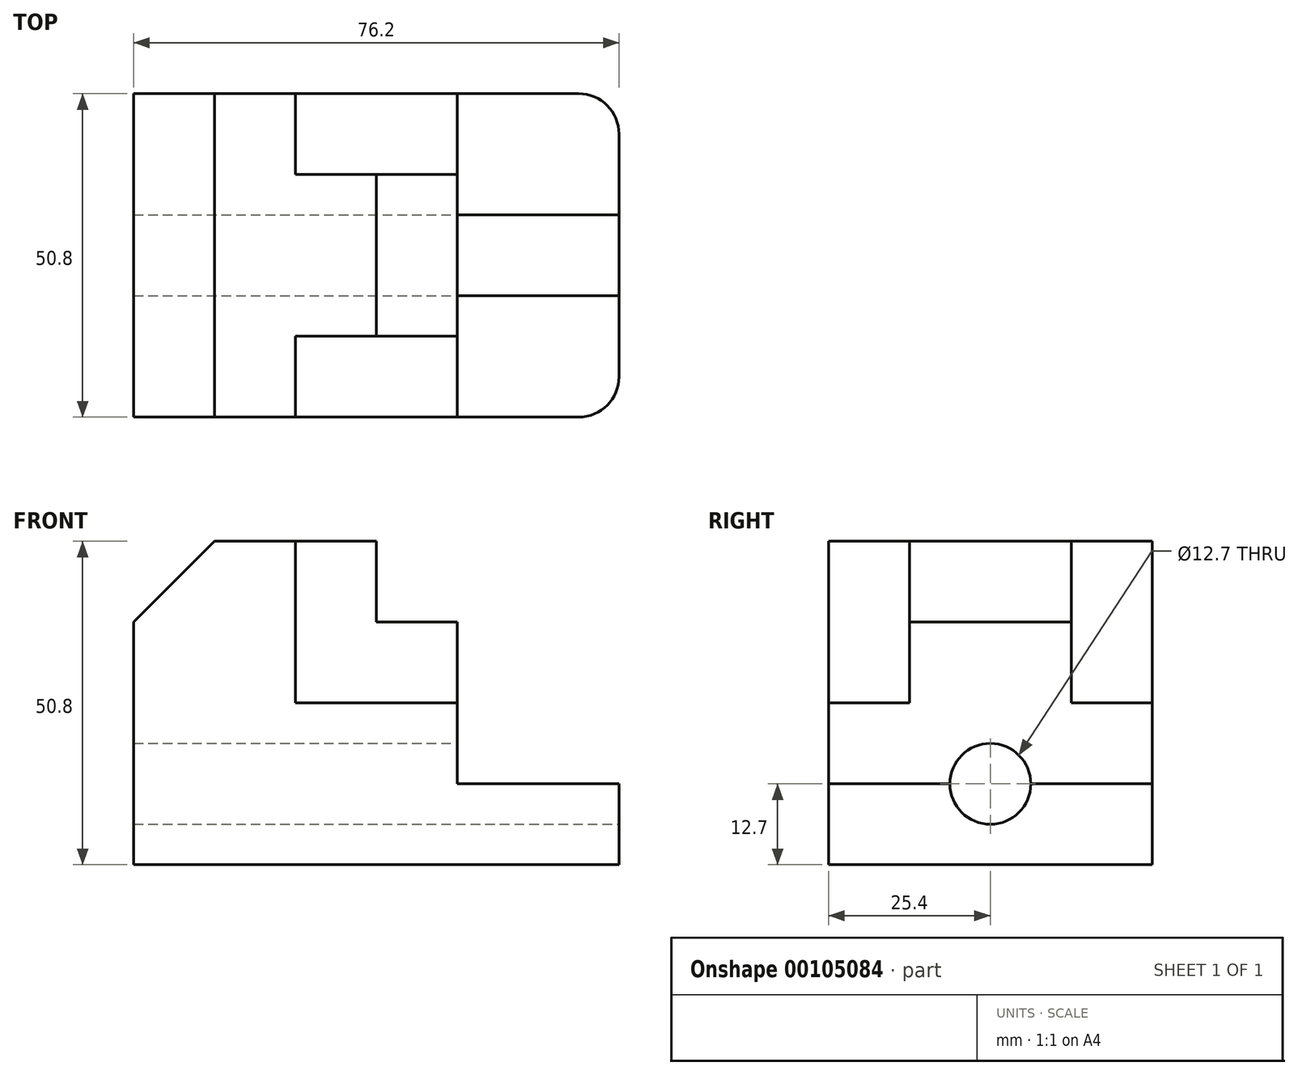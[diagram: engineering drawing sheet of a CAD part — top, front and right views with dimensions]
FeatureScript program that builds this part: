
annotation { "Feature Type Name" : "Feature", "Feature Type Description" : "" }
export const myFeature = defineFeature(function(context is Context, id is Id, definition is map)
    precondition{}
    {
        {
            var Q0;
            Q0=qCreatedBy(makeId("Front.planeOp"),FACE);
            var sketch = newSketch(context, id + "F0", { "sketchPlane" : qUnion([Q0])});
            skLineSegment(sketch, "E0.bottom", {"start": v(0, 0) * mm, "end": v(76.2, 0) * mm});
            skLineSegment(sketch, "E0.top", {"start": v(0, 50.8) * mm, "end": v(76.2, 50.8) * mm});
            skLineSegment(sketch, "E0.left", {"start": v(0, 0) * mm, "end": v(0, 50.8) * mm});
            skLineSegment(sketch, "E0.right", {"start": v(76.2, 0) * mm, "end": v(76.2, 50.8) * mm});
            skSolve(sketch);
        }
        {
            var Q0;
            Q0 = qSketchRegion(id + "F0", true);
            extrude(context, id + "F1", {"entities" : qUnion([Q0]), "depth" : 50.8 * mm});
        }
        {
            var Q0;
            Q0=makeQuery(id+"F1.opExtrude","CAP_FACE",FACE,{"disambiguationData":[OSD([sQuery(id+"F0.wireOp",EDGE,"E0.bottom"),sQuery(id+"F0.wireOp",EDGE,"E0.top"),sQuery(id+"F0.wireOp",EDGE,"E0.left"),sQuery(id+"F0.wireOp",EDGE,"E0.right")])],"isStart":false});
            var sketch = newSketch(context, id + "F2", { "sketchPlane" : qUnion([Q0])});
            skLineSegment(sketch, "E1", {"start": v(0, 50.8) * mm, "end": v(12.7, 50.8) * mm});
            skLineSegment(sketch, "E2", {"start": v(12.7, 50.8) * mm, "end": v(0, 38.1) * mm});
            skLineSegment(sketch, "E3", {"start": v(0, 38.1) * mm, "end": v(0, 50.8) * mm});
            skLineSegment(sketch, "E4", {"start": v(76.2, 50.8) * mm, "end": v(38.1, 50.8) * mm});
            skLineSegment(sketch, "E5", {"start": v(38.1, 50.8) * mm, "end": v(38.1, 38.1) * mm});
            skLineSegment(sketch, "E6", {"start": v(38.1, 38.1) * mm, "end": v(50.8, 38.1) * mm});
            skLineSegment(sketch, "E7", {"start": v(50.8, 38.1) * mm, "end": v(50.8, 12.7) * mm});
            skLineSegment(sketch, "E8", {"start": v(50.8, 12.7) * mm, "end": v(76.2, 12.7) * mm});
            skLineSegment(sketch, "E9", {"start": v(76.2, 12.7) * mm, "end": v(76.2, 50.8) * mm});
            skSolve(sketch);
        }
        {
            var Q0;
            Q0 = qSketchRegion(id + "F2", true);
            extrude(context, id + "F3", {"entities" : qUnion([Q0]), "operationType" : NewBodyOperationType.REMOVE, "endBound" : BoundingType.THROUGH_ALL, "oppositeDirection" : true, "depth" : 25.4 * mm});
        }
        {
            var Q0;
            Q0=makeQuery(id+"F1.opExtrude","CAP_FACE",FACE,{"disambiguationData":[OSD([sQuery(id+"F0.wireOp",EDGE,"E0.bottom"),sQuery(id+"F0.wireOp",EDGE,"E0.top"),sQuery(id+"F0.wireOp",EDGE,"E0.left"),sQuery(id+"F0.wireOp",EDGE,"E0.right")])],"isStart":false});
            var sketch = newSketch(context, id + "F4", { "sketchPlane" : qUnion([Q0])});
            skPoint(sketch, "E10.firstSnap0", {"position": v(25.4, 50.8) * mm});
            skPoint(sketch, "E10.oppositeSnap0", {"position": v(25.4, 50.8) * mm});
            skLineSegment(sketch, "E10.bottom", {"start": v(25.4, 25.4) * mm, "end": v(50.8, 25.4) * mm});
            skLineSegment(sketch, "E10.top", {"start": v(25.4, 50.8) * mm, "end": v(50.8, 50.8) * mm});
            skLineSegment(sketch, "E10.left", {"start": v(25.4, 25.4) * mm, "end": v(25.4, 50.8) * mm});
            skLineSegment(sketch, "E10.right", {"start": v(50.8, 25.4) * mm, "end": v(50.8, 50.8) * mm});
            skSolve(sketch);
        }
        {
            var Q0;
            {var subQ5=sQuery(id+"F4.wireOp",EDGE,"E10.bottom");Q0=makeQuery(id+"F4.imprint","IMPRINT",FACE,{"disambiguationData":[TD([[makeQuery(id+"F4.imprint","IMPRINT",EDGE,{"derivedFrom":subQ5}),1.0]])]});}
            extrude(context, id + "F5", {"entities" : qUnion([Q0]), "operationType" : NewBodyOperationType.REMOVE, "oppositeDirection" : true, "depth" : 12.7 * mm});
        }
        {
            var Q0;
            Q0=makeQuery(id+"F1.opExtrude","CAP_FACE",FACE,{"disambiguationData":[OSD([sQuery(id+"F0.wireOp",EDGE,"E0.bottom"),sQuery(id+"F0.wireOp",EDGE,"E0.top"),sQuery(id+"F0.wireOp",EDGE,"E0.left"),sQuery(id+"F0.wireOp",EDGE,"E0.right")])],"isStart":true});
            var sketch = newSketch(context, id + "F6", { "sketchPlane" : qUnion([Q0])});
            skLineSegment(sketch, "E11.bottom", {"start": v(-25.4, 50.8) * mm, "end": v(-50.8, 50.8) * mm});
            skLineSegment(sketch, "E11.top", {"start": v(-25.4, 25.4) * mm, "end": v(-50.8, 25.4) * mm});
            skLineSegment(sketch, "E11.left", {"start": v(-25.4, 50.8) * mm, "end": v(-25.4, 25.4) * mm});
            skLineSegment(sketch, "E11.right", {"start": v(-50.8, 50.8) * mm, "end": v(-50.8, 25.4) * mm});
            skSolve(sketch);
        }
        {
            var Q0;
            Q0 = qSketchRegion(id + "F6", true);
            extrude(context, id + "F7", {"entities" : qUnion([Q0]), "operationType" : NewBodyOperationType.REMOVE, "oppositeDirection" : true, "depth" : 12.7 * mm});
        }
        {
            var Q0;
            Q0=makeQuery(id+"F3.boolean.opBoolean","COPY",FACE,{"derivedFrom":makeQuery(id+"F3.opExtrude","SWEPT_FACE",FACE,{"disambiguationData":[OSD([sQuery(id+"F2.wireOp",EDGE,"E8")])]})});
            var sketch = newSketch(context, id + "F8", { "sketchPlane" : qUnion([Q0])});
            skLineSegment(sketch, "E12.bottom", {"start": v(50.8, -50.8) * mm, "end": v(69.85, -50.8) * mm});
            skLineSegment(sketch, "E12.top", {"start": v(50.8, 0) * mm, "end": v(69.85, 0) * mm});
            skLineSegment(sketch, "E12.left", {"start": v(50.8, -50.8) * mm, "end": v(50.8, 0) * mm});
            skLineSegment(sketch, "E12.right", {"start": v(76.2, -44.45) * mm, "end": v(76.2, -6.35) * mm});
            skPoint(sketch, "E13.visualSharp", {"position": v(76.2, -50.8) * mm});
            skArc(sketch, "E13.filletArc", {"start": v(69.85, -50.8) * mm, "mid": v(74.34, -48.94) * mm, "end": v(76.2, -44.45) * mm});
            skPoint(sketch, "E14.visualSharp", {"position": v(76.2, 0) * mm});
            skArc(sketch, "E14.filletArc", {"start": v(76.2, -6.35) * mm, "mid": v(74.34, -1.86) * mm, "end": v(69.85, 0) * mm});
            skSolve(sketch);
        }
        {
            var Q0;
            {var subQ0=sQuery(id+"F8.wireOp",EDGE,"E13.filletArc");Q0=makeQuery(id+"F8.imprint","IMPRINT",FACE,{"disambiguationData":[TD([[makeQuery(id+"F8.imprint","IMPRINT",EDGE,{"derivedFrom":subQ0}),-1.0]])]});}
            var Q1;
            {var subQ0=sQuery(id+"F8.wireOp",EDGE,"E14.filletArc");Q1=makeQuery(id+"F8.imprint","IMPRINT",FACE,{"disambiguationData":[TD([[makeQuery(id+"F8.imprint","IMPRINT",EDGE,{"derivedFrom":subQ0}),-1.0]])]});}
            extrude(context, id + "F9", {"entities" : qUnion([Q0, Q1]), "operationType" : NewBodyOperationType.REMOVE, "endBound" : BoundingType.THROUGH_ALL, "oppositeDirection" : true, "depth" : 25.4 * mm});
        }
        {
            var Q0;
            Q0=makeQuery(id+"F1.opExtrude","SWEPT_FACE",FACE,{"disambiguationData":[OSD([sQuery(id+"F0.wireOp",EDGE,"E0.right")])]});
            var sketch = newSketch(context, id + "F10", { "sketchPlane" : qUnion([Q0])});
            skCircle(sketch, "E15", {"center": v(-25.4, 12.7) * mm, "radius": 6.35 * mm});
            skLineSegment(sketch, "E16.bottom", {"start": v(-19.05, 19.05) * mm, "end": v(-31.75, 19.05) * mm});
            skLineSegment(sketch, "E16.top", {"start": v(-19.05, 6.35) * mm, "end": v(-31.75, 6.35) * mm});
            skLineSegment(sketch, "E16.left", {"start": v(-19.05, 19.05) * mm, "end": v(-19.05, 6.35) * mm});
            skLineSegment(sketch, "E16.right", {"start": v(-31.75, 19.05) * mm, "end": v(-31.75, 6.35) * mm});
            skSolve(sketch);
        }
        {
            var Q0;
            {var subQ0=sQuery(id+"F10.wireOp",EDGE,"E15");var subQ1=makeQuery(id+"F10.imprint","INTERSECT",VERTEX,{"derivedFrom":[subQ0,sQuery(id+"F10.wireOp",EDGE,"E16.top")]});Q0=makeQuery(id+"F10.imprint","IMPRINT",FACE,{"disambiguationData":[TD([[makeQuery(id+"F10.imprint","IMPRINT",EDGE,{"disambiguationData":[TD([[subQ1,1.0]])],"derivedFrom":subQ0}),1.0]])]});}
            var Q1;
            {var subQ0=sQuery(id+"F10.wireOp",EDGE,"E15");var subQ1=makeQuery(id+"F10.imprint","INTERSECT",VERTEX,{"derivedFrom":[subQ0,sQuery(id+"F10.wireOp",EDGE,"E16.bottom")]});Q1=makeQuery(id+"F10.imprint","IMPRINT",FACE,{"disambiguationData":[TD([[makeQuery(id+"F10.imprint","IMPRINT",EDGE,{"disambiguationData":[TD([[subQ1,1.0]])],"derivedFrom":subQ0}),1.0]])]});}
            extrude(context, id + "F11", {"entities" : qUnion([Q0, Q1]), "operationType" : NewBodyOperationType.REMOVE, "endBound" : BoundingType.THROUGH_ALL, "oppositeDirection" : true, "depth" : 25.4 * mm});
        }
    });
